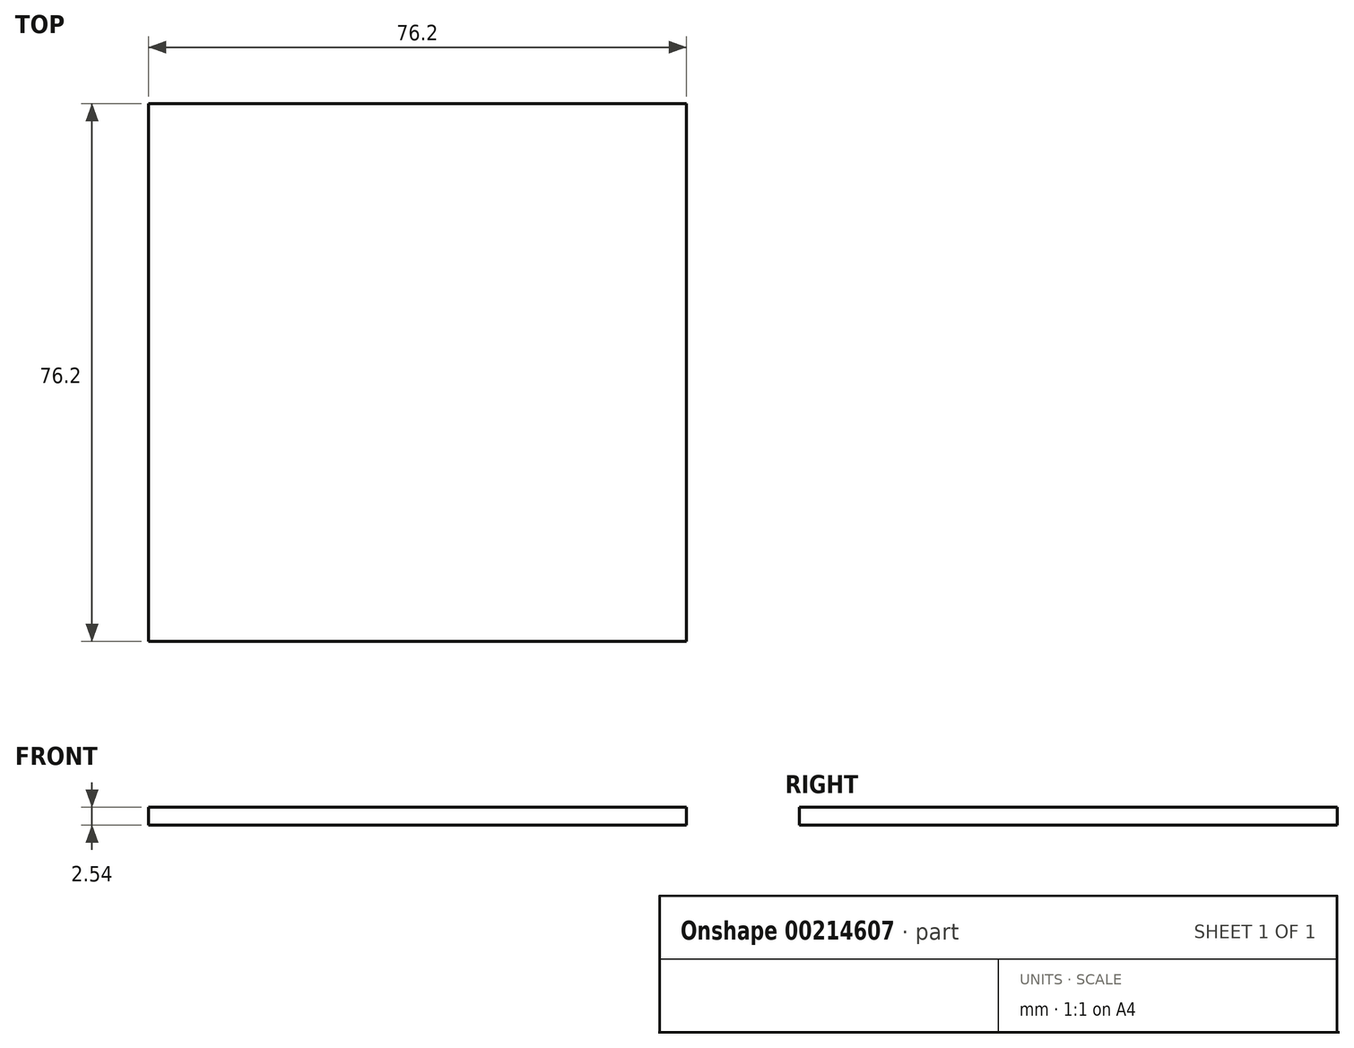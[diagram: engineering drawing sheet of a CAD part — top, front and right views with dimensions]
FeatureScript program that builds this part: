
annotation { "Feature Type Name" : "Feature", "Feature Type Description" : "" }
export const myFeature = defineFeature(function(context is Context, id is Id, definition is map)
    precondition{}
    {
        {
            var Q0;
            Q0=qCreatedBy(makeId("Top.planeOp"),FACE);
            var sketch = newSketch(context, id + "F0", { "sketchPlane" : qUnion([Q0])});
            skLineSegment(sketch, "E0.bottom", {"start": v(-32.36, 35.35) * mm, "end": v(43.84, 35.35) * mm});
            skLineSegment(sketch, "E0.top", {"start": v(-32.36, -40.85) * mm, "end": v(43.84, -40.85) * mm});
            skLineSegment(sketch, "E0.left", {"start": v(-32.36, 35.35) * mm, "end": v(-32.36, -40.85) * mm});
            skLineSegment(sketch, "E0.right", {"start": v(43.84, 35.35) * mm, "end": v(43.84, -40.85) * mm});
            skSolve(sketch);
        }
        {
            var Q0;
            Q0=makeQuery(id+"F0.imprint","IMPRINT",FACE,{"disambiguationData":[TD([[makeQuery(id+"F0.imprint","IMPRINT",EDGE,{"derivedFrom":sQuery(id+"F0.wireOp",EDGE,"E0.bottom")}),-1.0]])]});
            extrude(context, id + "F1", {"entities" : qUnion([Q0]), "depth" : 2.54 * mm});
        }
    });
